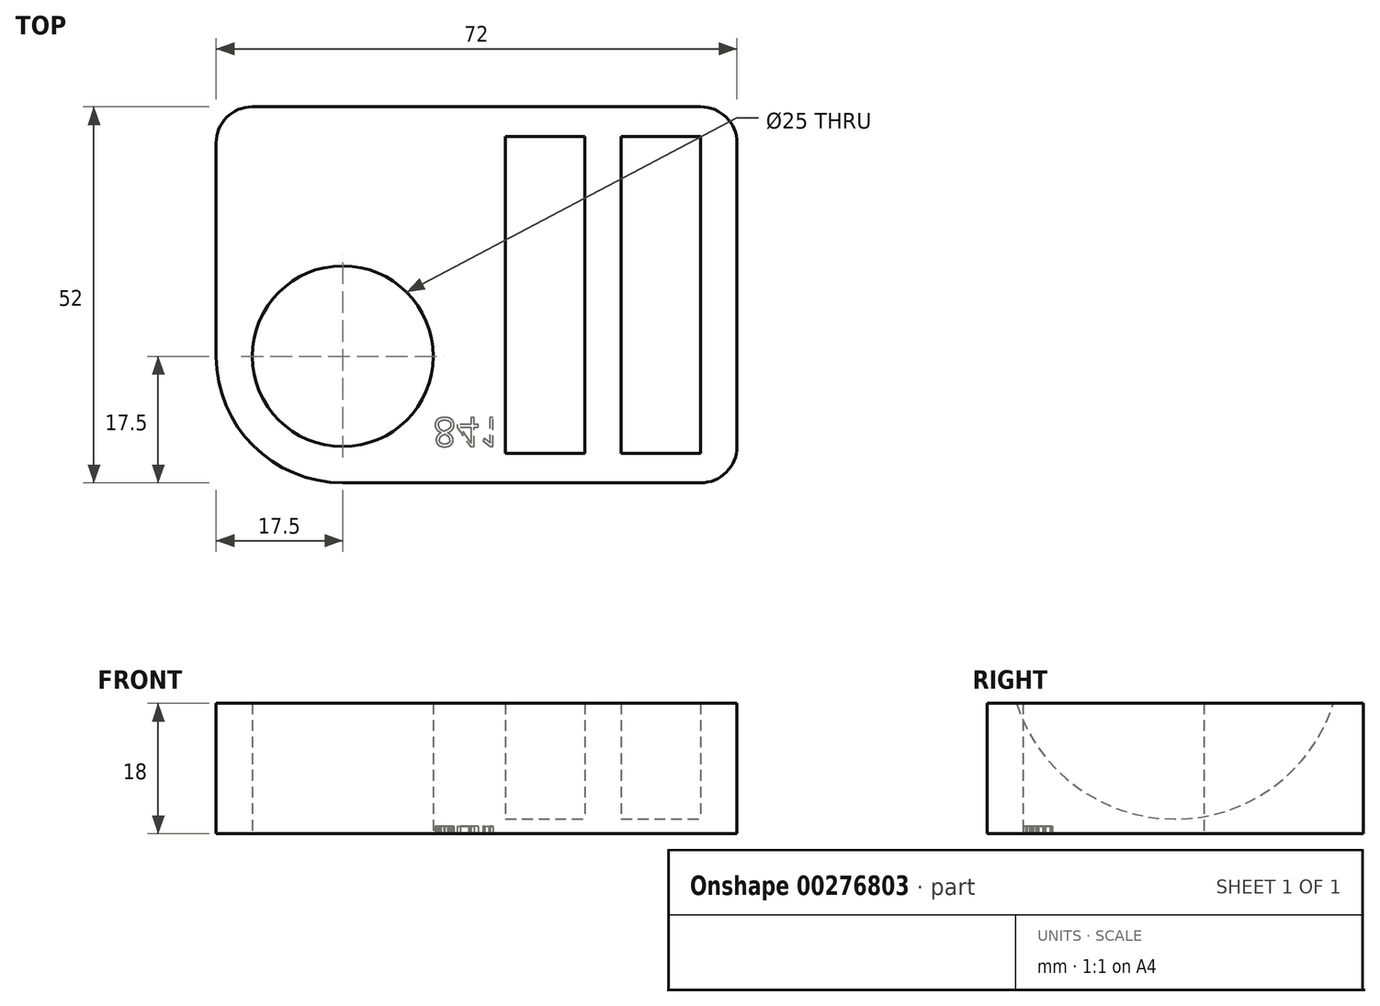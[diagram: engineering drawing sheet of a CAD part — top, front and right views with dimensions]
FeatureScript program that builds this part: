
annotation { "Feature Type Name" : "Feature", "Feature Type Description" : "" }
export const myFeature = defineFeature(function(context is Context, id is Id, definition is map)
    precondition{}
    {
        {
            var Q0;
            Q0=qCreatedBy(makeId("Top.planeOp"),FACE);
            var sketch = newSketch(context, id + "F0", { "sketchPlane" : qUnion([Q0])});
            skLineSegment(sketch, "E0.bottom", {"start": v(17.5, 0) * mm, "end": v(67, 0) * mm});
            skLineSegment(sketch, "E0.top", {"start": v(5, 52) * mm, "end": v(67, 52) * mm});
            skLineSegment(sketch, "E0.left", {"start": v(0, 17.5) * mm, "end": v(0, 47) * mm});
            skLineSegment(sketch, "E0.right", {"start": v(72, 5) * mm, "end": v(72, 47) * mm});
            skLineSegment(sketch, "E1.bottom", {"start": v(0, 0) * mm, "end": v(17.5, 0) * mm, "construction": true});
            skLineSegment(sketch, "E1.top", {"start": v(0, 17.5) * mm, "end": v(17.5, 17.5) * mm, "construction": true});
            skLineSegment(sketch, "E1.left", {"start": v(0, 0) * mm, "end": v(0, 17.5) * mm, "construction": true});
            skLineSegment(sketch, "E1.right", {"start": v(17.5, 0) * mm, "end": v(17.5, 17.5) * mm, "construction": true});
            skCircle(sketch, "E2", {"center": v(17.5, 17.5) * mm, "radius": 12.5 * mm});
            skPoint(sketch, "E3.visualSharp", {"position": v(0, 0) * mm});
            skArc(sketch, "E3.filletArc", {"start": v(0, 17.5) * mm, "mid": v(5.13, 5.13) * mm, "end": v(17.5, 0) * mm});
            skPoint(sketch, "E4.visualSharp", {"position": v(0, 52) * mm});
            skArc(sketch, "E4.filletArc", {"start": v(5, 52) * mm, "mid": v(1.46, 50.54) * mm, "end": v(0, 47) * mm});
            skPoint(sketch, "E5.visualSharp", {"position": v(72, 52) * mm});
            skArc(sketch, "E5.filletArc", {"start": v(72, 47) * mm, "mid": v(70.54, 50.54) * mm, "end": v(67, 52) * mm});
            skPoint(sketch, "E6.visualSharp", {"position": v(72, 0) * mm});
            skArc(sketch, "E6.filletArc", {"start": v(67, 0) * mm, "mid": v(70.54, 1.46) * mm, "end": v(72, 5) * mm});
            skSolve(sketch);
        }
        {
            var Q0;
            Q0=makeQuery(id+"F0.imprint","IMPRINT",FACE,{"disambiguationData":[TD([[makeQuery(id+"F0.imprint","IMPRINT",EDGE,{"derivedFrom":sQuery(id+"F0.wireOp",EDGE,"E0.bottom")}),1.0]])]});
            extrude(context, id + "F1", {"entities" : qUnion([Q0]), "depth" : 25 * mm});
        }
        {
            var Q0;
            Q0=makeQuery(id+"F1.opExtrude","CAP_FACE",FACE,{"disambiguationData":[OSD([sQuery(id+"F0.wireOp",EDGE,"E0.bottom"),sQuery(id+"F0.wireOp",EDGE,"E0.top"),sQuery(id+"F0.wireOp",EDGE,"E0.right"),sQuery(id+"F0.wireOp",EDGE,"E2"),sQuery(id+"F0.wireOp",EDGE,"E3.filletArc"),sQuery(id+"F0.wireOp",EDGE,"E4.filletArc"),sQuery(id+"F0.wireOp",EDGE,"E5.filletArc"),sQuery(id+"F0.wireOp",EDGE,"E6.filletArc")])],"isStart":false});
            var sketch = newSketch(context, id + "F2", { "sketchPlane" : qUnion([Q0])});
            skLineSegment(sketch, "E7.bottom", {"start": v(0, 0) * mm, "end": v(40, 0) * mm, "construction": true});
            skLineSegment(sketch, "E7.top", {"start": v(0, 26) * mm, "end": v(40, 26) * mm, "construction": true});
            skLineSegment(sketch, "E7.left", {"start": v(0, 0) * mm, "end": v(0, 26) * mm, "construction": true});
            skLineSegment(sketch, "E7.right", {"start": v(40, 0) * mm, "end": v(40, 26) * mm, "construction": true});
            skLineSegment(sketch, "E8.bottom", {"start": v(40, 26) * mm, "end": v(51, 26) * mm});
            skLineSegment(sketch, "E8.top", {"start": v(40, 3) * mm, "end": v(51, 3) * mm});
            skLineSegment(sketch, "E8.left", {"start": v(40, 26) * mm, "end": v(40, 3) * mm});
            skLineSegment(sketch, "E8.right", {"start": v(51, 26) * mm, "end": v(51, 3) * mm});
            skLineSegment(sketch, "E9", {"start": v(51, 26) * mm, "end": v(56, 26) * mm, "construction": true});
            skLineSegment(sketch, "E10.bottom", {"start": v(56, 26) * mm, "end": v(67, 26) * mm});
            skLineSegment(sketch, "E10.top", {"start": v(56, 3) * mm, "end": v(67, 3) * mm});
            skLineSegment(sketch, "E10.left", {"start": v(56, 26) * mm, "end": v(56, 3) * mm});
            skLineSegment(sketch, "E10.right", {"start": v(67, 26) * mm, "end": v(67, 3) * mm});
            skSolve(sketch);
        }
        {
            var Q0;
            Q0=makeQuery(id+"F2.imprint","IMPRINT",FACE,{"disambiguationData":[TD([[makeQuery(id+"F2.imprint","IMPRINT",EDGE,{"derivedFrom":sQuery(id+"F2.wireOp",EDGE,"E8.bottom")}),-1.0]])]});
            var Q1;
            Q1=makeQuery(id+"F2.imprint","IMPRINT",FACE,{"disambiguationData":[TD([[makeQuery(id+"F2.imprint","IMPRINT",EDGE,{"derivedFrom":sQuery(id+"F2.wireOp",EDGE,"E10.bottom")}),-1.0]])]});
            var Q2;
            Q2=sQuery(id+"F2.wireOp",EDGE,"E8.bottom");
            revolve(context, id + "F3", {"operationType" : NewBodyOperationType.REMOVE, "entities" : qUnion([Q0, Q1]), "axis" : qUnion([Q2]), "revolveType" : RevolveType.FULL, "oppositeDirection" : true});
        }
        {
            var Q0;
            Q0=makeQuery(id+"F1.opExtrude","SWEPT_FACE",FACE,{"disambiguationData":[OSD([sQuery(id+"F0.wireOp",EDGE,"E0.bottom")])]});
            var sketch = newSketch(context, id + "F4", { "sketchPlane" : qUnion([Q0])});
            skLineSegment(sketch, "E11", {"start": v(0, 0) * mm, "end": v(0, 18) * mm, "construction": true});
            skLineSegment(sketch, "E12.bottom", {"start": v(0, 18) * mm, "end": v(82.21, 18) * mm});
            skLineSegment(sketch, "E12.top", {"start": v(0, 36.05) * mm, "end": v(82.21, 36.05) * mm});
            skLineSegment(sketch, "E12.left", {"start": v(0, 18) * mm, "end": v(0, 36.05) * mm});
            skLineSegment(sketch, "E12.right", {"start": v(82.21, 18) * mm, "end": v(82.21, 36.05) * mm});
            skSolve(sketch);
        }
        {
            var Q0;
            Q0=qSketchRegion(id+"F4",true);
            extrude(context, id + "F5", {"entities" : qUnion([Q0]), "operationType" : NewBodyOperationType.REMOVE, "endBound" : BoundingType.THROUGH_ALL, "oppositeDirection" : true, "depth" : 25 * mm});
        }
        {
            var Q0;
            Q0=makeQuery(id+"F1.opExtrude","CAP_FACE",FACE,{"disambiguationData":[OSD([sQuery(id+"F0.wireOp",EDGE,"E0.bottom"),sQuery(id+"F0.wireOp",EDGE,"E0.top"),sQuery(id+"F0.wireOp",EDGE,"E0.left"),sQuery(id+"F0.wireOp",EDGE,"E0.right"),sQuery(id+"F0.wireOp",EDGE,"E2"),sQuery(id+"F0.wireOp",EDGE,"E3.filletArc"),sQuery(id+"F0.wireOp",EDGE,"E4.filletArc"),sQuery(id+"F0.wireOp",EDGE,"E5.filletArc"),sQuery(id+"F0.wireOp",EDGE,"E6.filletArc")])],"isStart":true});
            var sketch = newSketch(context, id + "F6", { "sketchPlane" : qUnion([Q0])});
            skLineSegment(sketch, "E13.bottom", {"start": v(0, 0) * mm, "end": v(30, 0) * mm, "construction": true});
            skLineSegment(sketch, "E13.top", {"start": v(0, -5) * mm, "end": v(30, -5) * mm, "construction": true});
            skLineSegment(sketch, "E13.left", {"start": v(0, 0) * mm, "end": v(0, -5) * mm, "construction": true});
            skLineSegment(sketch, "E13.right", {"start": v(30, 0) * mm, "end": v(30, -5) * mm, "construction": true});
            skText(sketch, "E14", { "text": "841\n", "fontName": "OpenSans-Regular.ttf"});
            const initialGuessF6  = {"E14": [0.03, -0.009, 1, 0, 0.004]};
            skSetInitialGuess(sketch, initialGuessF6);
            skSolve(sketch);
        }
        {
            var Q0;
            Q0 = qSketchRegion(id + "F6", true);
            extrude(context, id + "F7", {"entities" : qUnion([Q0]), "operationType" : NewBodyOperationType.REMOVE, "oppositeDirection" : true, "depth" : 1 * mm});
        }
    });
